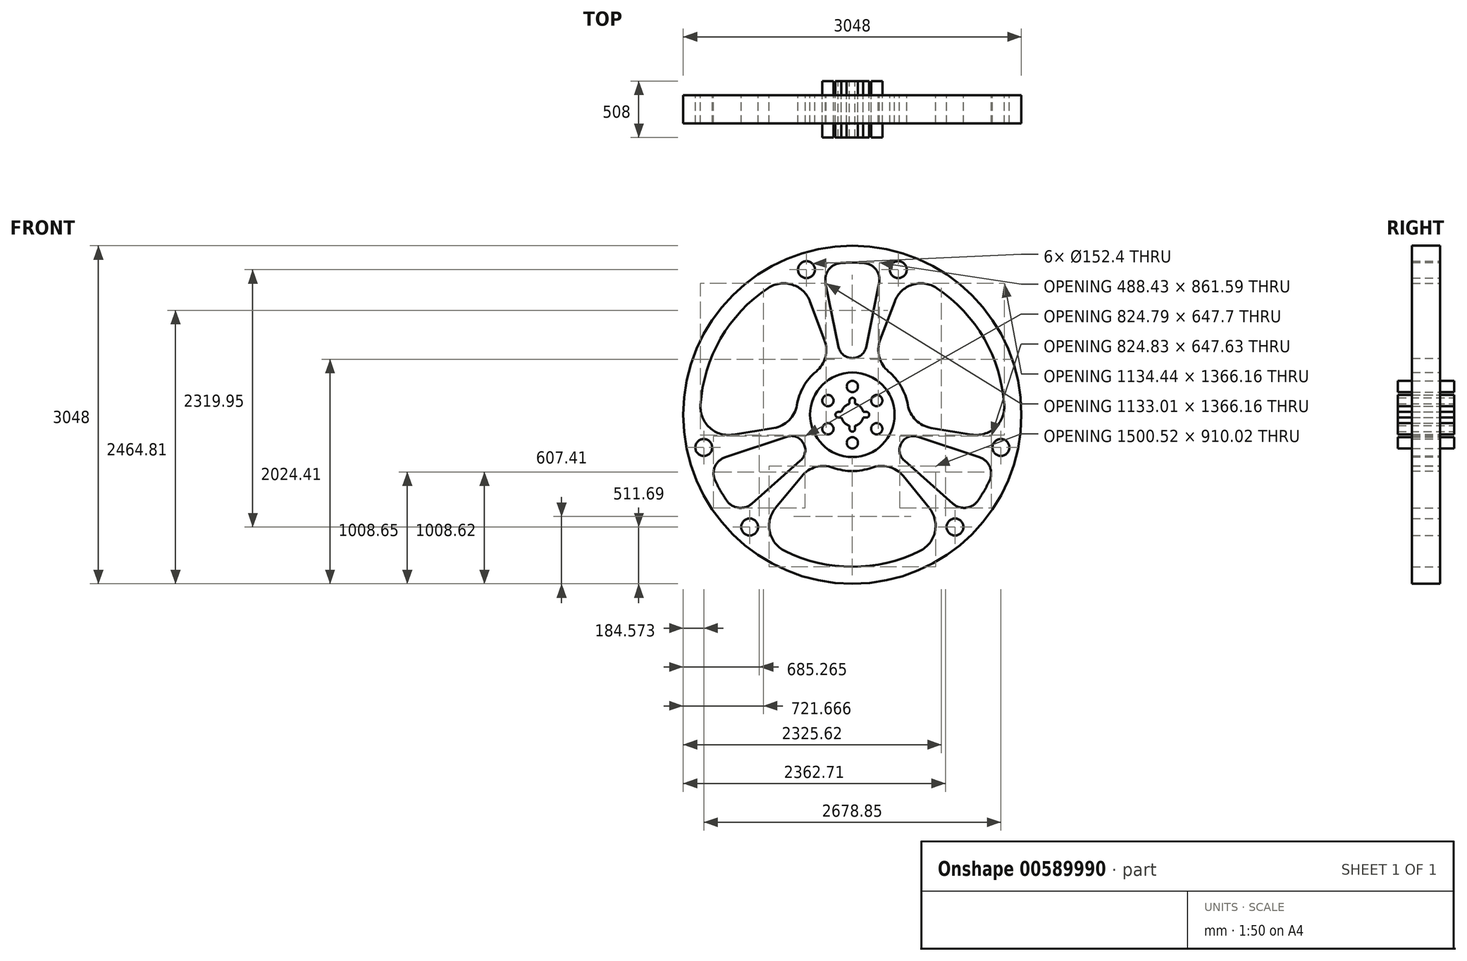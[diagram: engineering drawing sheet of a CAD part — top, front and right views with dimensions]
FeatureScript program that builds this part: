
annotation { "Feature Type Name" : "Feature", "Feature Type Description" : "" }
export const myFeature = defineFeature(function(context is Context, id is Id, definition is map)
    precondition{}
    {
        {
            var Q0;
            Q0=qCreatedBy(makeId("Front.planeOp"),FACE);
            var sketch = newSketch(context, id + "F0", { "sketchPlane" : qUnion([Q0])});
            skCircle(sketch, "E0", {"center": v(0, 0) * mm, "radius": 1524 * mm});
            skArc(sketch, "E1", {"start": v(103.3, 1367.7) * mm, "mid": v(0, 1371.6) * mm, "end": v(-103.3, 1367.7) * mm});
            skArc(sketch, "E2", {"start": v(-173.99, -477.28) * mm, "mid": v(0, -508) * mm, "end": v(173.99, -477.28) * mm});
            skCircle(sketch, "E3", {"center": v(0, 0) * mm, "radius": 381 * mm});
            skArc(sketch, "E4", {"start": v(-173.99, -477.28) * mm, "mid": v(-327.73, -470.84) * mm, "end": v(-456.97, -554.35) * mm});
            skArc(sketch, "E5", {"start": v(609.08, -1228.95) * mm, "mid": v(744.67, -1054.47) * mm, "end": v(692.28, -839.8) * mm});
            skArc(sketch, "E6.trimOffspring", {"start": v(-692.28, -839.8) * mm, "mid": v(-744.67, -1054.47) * mm, "end": v(-609.08, -1228.95) * mm});
            skArc(sketch, "E7.trimOffspring", {"start": v(458.29, -553.27) * mm, "mid": v(328.26, -469.9) * mm, "end": v(173.99, -477.28) * mm});
            skLineSegment(sketch, "E8.trimOffspring", {"start": v(458.29, -553.27) * mm, "end": v(692.28, -839.8) * mm});
            skLineSegment(sketch, "E9.trimOffspring", {"start": v(-456.97, -554.35) * mm, "end": v(-692.28, -839.8) * mm});
            skArc(sketch, "E10", {"start": v(241.17, 1185.35) * mm, "mid": v(213.4, 1307.65) * mm, "end": v(103.3, 1367.7) * mm});
            skArc(sketch, "E11.trimOffspring", {"start": v(-103.3, 1367.7) * mm, "mid": v(-213.39, 1307.65) * mm, "end": v(-241.16, 1185.35) * mm});
            skArc(sketch, "E12", {"start": v(-124.4, 611.7) * mm, "mid": v(0.04, 510.01) * mm, "end": v(124.5, 611.7) * mm});
            skLineSegment(sketch, "E13.trimOffspring", {"start": v(124.5, 611.7) * mm, "end": v(241.17, 1185.35) * mm});
            skLineSegment(sketch, "E14.trimOffspring", {"start": v(-124.4, 611.7) * mm, "end": v(-241.16, 1185.35) * mm});
            skArc(sketch, "E15.trimOffspring", {"start": v(-609.08, -1228.95) * mm, "mid": v(0, -1371.6) * mm, "end": v(609.08, -1228.95) * mm});
            skArc(sketch, "E16.1.0", {"start": v(-1236.12, -594.39) * mm, "mid": v(-1187.84, -685.8) * mm, "end": v(-1132.82, -773.31) * mm});
            skArc(sketch, "E16.1.1", {"start": v(-1132.82, -773.31) * mm, "mid": v(-1025.76, -838.62) * mm, "end": v(-905.96, -801.53) * mm});
            skLineSegment(sketch, "E16.1.2", {"start": v(-467.54, -413.59) * mm, "end": v(-905.96, -801.53) * mm});
            skArc(sketch, "E16.1.3", {"start": v(-467.54, -413.59) * mm, "mid": v(-441.7, -254.97) * mm, "end": v(-591.99, -198.03) * mm});
            skArc(sketch, "E16.2.0", {"start": v(1132.81, -773.32) * mm, "mid": v(1187.84, -685.8) * mm, "end": v(1236.12, -594.4) * mm});
            skArc(sketch, "E16.2.1", {"start": v(1236.12, -594.4) * mm, "mid": v(1239.15, -469.02) * mm, "end": v(1147.13, -383.82) * mm});
            skLineSegment(sketch, "E16.2.2", {"start": v(591.95, -198.1) * mm, "end": v(1147.13, -383.82) * mm});
            skArc(sketch, "E16.2.3", {"start": v(591.95, -198.1) * mm, "mid": v(441.66, -255.04) * mm, "end": v(467.5, -413.66) * mm});
            skLineSegment(sketch, "E17.1.0", {"start": v(-591.99, -198.03) * mm, "end": v(-1147.13, -383.82) * mm});
            skArc(sketch, "E17.1.1", {"start": v(-1147.13, -383.82) * mm, "mid": v(-1239.15, -469.02) * mm, "end": v(-1236.12, -594.39) * mm});
            skLineSegment(sketch, "E17.2.0", {"start": v(467.5, -413.66) * mm, "end": v(905.96, -801.53) * mm});
            skArc(sketch, "E17.2.1", {"start": v(905.96, -801.53) * mm, "mid": v(1025.76, -838.63) * mm, "end": v(1132.81, -773.32) * mm});
            skArc(sketch, "E18.1.0", {"start": v(250, 673.52) * mm, "mid": v(242.82, 519.24) * mm, "end": v(326.34, 389.31) * mm});
            skLineSegment(sketch, "E18.1.1", {"start": v(250, 673.52) * mm, "end": v(381.15, 1019.43) * mm});
            skArc(sketch, "E18.1.2", {"start": v(759.76, 1141.95) * mm, "mid": v(540.86, 1172.14) * mm, "end": v(381.15, 1019.43) * mm});
            skArc(sketch, "E18.1.3", {"start": v(1368.84, 87) * mm, "mid": v(1187.84, 685.8) * mm, "end": v(759.76, 1141.95) * mm});
            skArc(sketch, "E18.1.4", {"start": v(1073.43, -179.63) * mm, "mid": v(1285.53, -117.67) * mm, "end": v(1368.84, 87) * mm});
            skLineSegment(sketch, "E18.1.5", {"start": v(708.57, -118.57) * mm, "end": v(1073.43, -179.63) * mm});
            skArc(sketch, "E18.1.6", {"start": v(500.33, 87.96) * mm, "mid": v(571.62, -48.4) * mm, "end": v(708.57, -118.57) * mm});
            skArc(sketch, "E18.1.7", {"start": v(500.33, 87.96) * mm, "mid": v(439.94, 254) * mm, "end": v(326.34, 389.31) * mm});
            skArc(sketch, "E18.2.0", {"start": v(-708.29, -120.26) * mm, "mid": v(-571.08, -49.33) * mm, "end": v(-500.33, 87.96) * mm});
            skLineSegment(sketch, "E18.2.1", {"start": v(-708.29, -120.26) * mm, "end": v(-1073.43, -179.63) * mm});
            skArc(sketch, "E18.2.2", {"start": v(-1368.84, 87) * mm, "mid": v(-1285.53, -117.67) * mm, "end": v(-1073.43, -179.63) * mm});
            skArc(sketch, "E18.2.3", {"start": v(-759.76, 1141.95) * mm, "mid": v(-1187.84, 685.8) * mm, "end": v(-1368.84, 87) * mm});
            skArc(sketch, "E18.2.4", {"start": v(-381.15, 1019.43) * mm, "mid": v(-540.86, 1172.14) * mm, "end": v(-759.76, 1141.95) * mm});
            skLineSegment(sketch, "E18.2.5", {"start": v(-251.6, 672.92) * mm, "end": v(-381.15, 1019.43) * mm});
            skArc(sketch, "E18.2.6", {"start": v(-326.34, 389.31) * mm, "mid": v(-243.9, 519.24) * mm, "end": v(-251.6, 672.92) * mm});
            skArc(sketch, "E18.2.7", {"start": v(-326.34, 389.31) * mm, "mid": v(-439.94, 254) * mm, "end": v(-500.33, 87.96) * mm});
            skCircle(sketch, "E19", {"center": v(-413.94, 1307.65) * mm, "radius": 76.2 * mm});
            skPoint(sketch, "E19.centerSnap0", {"position": v(-213.39, 1307.65) * mm});
            skCircle(sketch, "E20", {"center": v(413.95, 1307.65) * mm, "radius": 76.2 * mm});
            skPoint(sketch, "E20.centerSnap0", {"position": v(213.4, 1307.65) * mm});
            skCircle(sketch, "E21.1.0", {"center": v(-925.48, -1012.3) * mm, "radius": 76.2 * mm});
            skCircle(sketch, "E21.1.1", {"center": v(-1339.43, -295.34) * mm, "radius": 76.2 * mm});
            skCircle(sketch, "E21.2.0", {"center": v(1339.43, -295.34) * mm, "radius": 76.2 * mm});
            skCircle(sketch, "E21.2.1", {"center": v(925.48, -1012.3) * mm, "radius": 76.2 * mm});
            skArc(sketch, "E22", {"start": v(-25.4, 98.37) * mm, "mid": v(-71.84, 71.84) * mm, "end": v(-98.37, 25.4) * mm});
            skLineSegment(sketch, "E23", {"start": v(25.4, 98.37) * mm, "end": v(25.4, 127) * mm});
            skLineSegment(sketch, "E24", {"start": v(-25.4, 98.37) * mm, "end": v(-25.4, 127) * mm});
            skLineSegment(sketch, "E25", {"start": v(-25.4, -98.37) * mm, "end": v(-25.4, -127) * mm});
            skLineSegment(sketch, "E26", {"start": v(25.4, -98.37) * mm, "end": v(25.4, -127) * mm});
            skArc(sketch, "E27", {"start": v(25.4, 127) * mm, "mid": v(0, 152.4) * mm, "end": v(-25.4, 127) * mm});
            skArc(sketch, "E28", {"start": v(-25.4, -127) * mm, "mid": v(0, -152.4) * mm, "end": v(25.4, -127) * mm});
            skArc(sketch, "E29.trimOffspring", {"start": v(25.4, -98.37) * mm, "mid": v(71.84, -71.84) * mm, "end": v(98.37, -25.4) * mm});
            skPoint(sketch, "E30.end.orphan", {"position": v(-25.4, 0) * mm});
            skLineSegment(sketch, "E31", {"start": v(-98.37, -25.4) * mm, "end": v(-127.4, -25.4) * mm});
            skLineSegment(sketch, "E32", {"start": v(-98.37, 25.4) * mm, "end": v(-127, 25.4) * mm});
            skLineSegment(sketch, "E33", {"start": v(98.37, 25.4) * mm, "end": v(127, 25.4) * mm});
            skLineSegment(sketch, "E34", {"start": v(98.37, -25.4) * mm, "end": v(127, -25.4) * mm});
            skArc(sketch, "E35", {"start": v(-127, 25.4) * mm, "mid": v(-152.4, 0.2) * mm, "end": v(-127.4, -25.4) * mm});
            skArc(sketch, "E36", {"start": v(127, -25.4) * mm, "mid": v(152.4, 0) * mm, "end": v(127, 25.4) * mm});
            skArc(sketch, "E37.trimOffspring", {"start": v(-98.37, -25.4) * mm, "mid": v(-71.84, -71.84) * mm, "end": v(-25.4, -98.37) * mm});
            skArc(sketch, "E38.trimOffspring", {"start": v(98.37, 25.4) * mm, "mid": v(71.84, 71.84) * mm, "end": v(25.4, 98.37) * mm});
            skCircle(sketch, "E39", {"center": v(0, -254) * mm, "radius": 50.8 * mm});
            skCircle(sketch, "E40", {"center": v(0, 254) * mm, "radius": 50.8 * mm});
            skCircle(sketch, "E41.1.0", {"center": v(-219.97, -127) * mm, "radius": 50.8 * mm});
            skCircle(sketch, "E41.2.0", {"center": v(219.97, -127) * mm, "radius": 50.8 * mm});
            skCircle(sketch, "E42.1.0", {"center": v(219.97, 127) * mm, "radius": 50.8 * mm});
            skCircle(sketch, "E42.2.0", {"center": v(-219.97, 127) * mm, "radius": 50.8 * mm});
            skSolve(sketch);
        }
        {
            var Q0;
            Q0=makeQuery(id+"F0.imprint","IMPRINT",FACE,{"disambiguationData":[TD([[makeQuery(id+"F0.imprint","IMPRINT",EDGE,{"derivedFrom":sQuery(id+"F0.wireOp",EDGE,"E0")}),1.0]])]});
            extrude(context, id + "F1", {"entities" : qUnion([Q0]), "depth" : 254 * mm, "offsetDistance" : 25.4 * mm, "symmetric" : true});
        }
        {
            var Q0;
            Q0=makeQuery(id+"F0.imprint","IMPRINT",FACE,{"disambiguationData":[TD([[makeQuery(id+"F0.imprint","IMPRINT",EDGE,{"derivedFrom":sQuery(id+"F0.wireOp",EDGE,"E22")}),1.0]])]});
            var Q1;
            Q1=makeQuery(id+"F0.imprint","IMPRINT",FACE,{"disambiguationData":[TD([[makeQuery(id+"F0.imprint","IMPRINT",EDGE,{"derivedFrom":sQuery(id+"F0.wireOp",EDGE,"E40")}),1.0]])]});
            var Q2;
            Q2=makeQuery(id+"F0.imprint","IMPRINT",FACE,{"disambiguationData":[TD([[makeQuery(id+"F0.imprint","IMPRINT",EDGE,{"derivedFrom":sQuery(id+"F0.wireOp",EDGE,"E42.2.0")}),1.0]])]});
            var Q3;
            Q3=makeQuery(id+"F0.imprint","IMPRINT",FACE,{"disambiguationData":[TD([[makeQuery(id+"F0.imprint","IMPRINT",EDGE,{"derivedFrom":sQuery(id+"F0.wireOp",EDGE,"E41.1.0")}),1.0]])]});
            var Q4;
            Q4=makeQuery(id+"F0.imprint","IMPRINT",FACE,{"disambiguationData":[TD([[makeQuery(id+"F0.imprint","IMPRINT",EDGE,{"derivedFrom":sQuery(id+"F0.wireOp",EDGE,"E39")}),1.0]])]});
            var Q5;
            Q5=makeQuery(id+"F0.imprint","IMPRINT",FACE,{"disambiguationData":[TD([[makeQuery(id+"F0.imprint","IMPRINT",EDGE,{"derivedFrom":sQuery(id+"F0.wireOp",EDGE,"E41.2.0")}),1.0]])]});
            var Q6;
            Q6=makeQuery(id+"F0.imprint","IMPRINT",FACE,{"disambiguationData":[TD([[makeQuery(id+"F0.imprint","IMPRINT",EDGE,{"derivedFrom":sQuery(id+"F0.wireOp",EDGE,"E42.1.0")}),1.0]])]});
            extrude(context, id + "F2", {"entities" : qUnion([Q0, Q1, Q2, Q3, Q4, Q5, Q6]), "depth" : 508 * mm, "offsetDistance" : 25.4 * mm, "symmetric" : true});
        }
    });
